# Revit family: Furniture-Lighted_Medicine_Cabinet-KOHLER-Grooming-K-33691K_1
name_source: partatom
category: Lighting Fixtures
units: mm (PartAtom-declared; Revit-internal decimal feet)

## family parameters
Cut with Voids When Loaded = No
Host = Face
Light Source = Yes
OmniClass Number = 23.25.53.11.13.11
OmniClass Title = Medicine Cabinet
Part Type = Normal
Room Calculation Point = No
Round Connector Dimension = Use Diameter
Shared = No

## types (1)
- NA-Black
    ADA Compliant = No
    Apparent Load = 55 VA
    Assembly Code = E2010
    Color Filter = 16777215
    Date Modified = 05/25/2023
    Default Elevation = 60"
    Depth = 6 5/8"
    Description = 900 MM Lighted 600 MM Cabinet With 300 MM Basic Side Cabinet
    Dimming Lamp Color Temperature Shift = Incandescent Lamp Curve
    Electrical Connector = Yes
    Electrical Note = One Dedicated Circuit Required
    Emit from Line Length = 24"
    Finish = Kohler-Metal-NA-Black
    Hardware Included = No
    Height = 31 11/16"
    Lamp = LED
    Light Source Symbol Size = 3 15/16"
    Manufacturer = Kohler Co.
    Master Format 2014 = 41 53 13
    Master Format 2014 Name = Storage Cabinets
    Material = Aluminium
    Model = K-33691K-NA
    Product Name = Grooming
    Type = 1
    URL = https://www.kohlerasiapacific.com
    Voltage = 240 V
    WaterSense Certified = No
    Wattage Comments = 55W
    Width = 35 3/16"

## geometry (parser evidence)
native form markers: Sweep x7
no freeform markers — native parametric forms only
